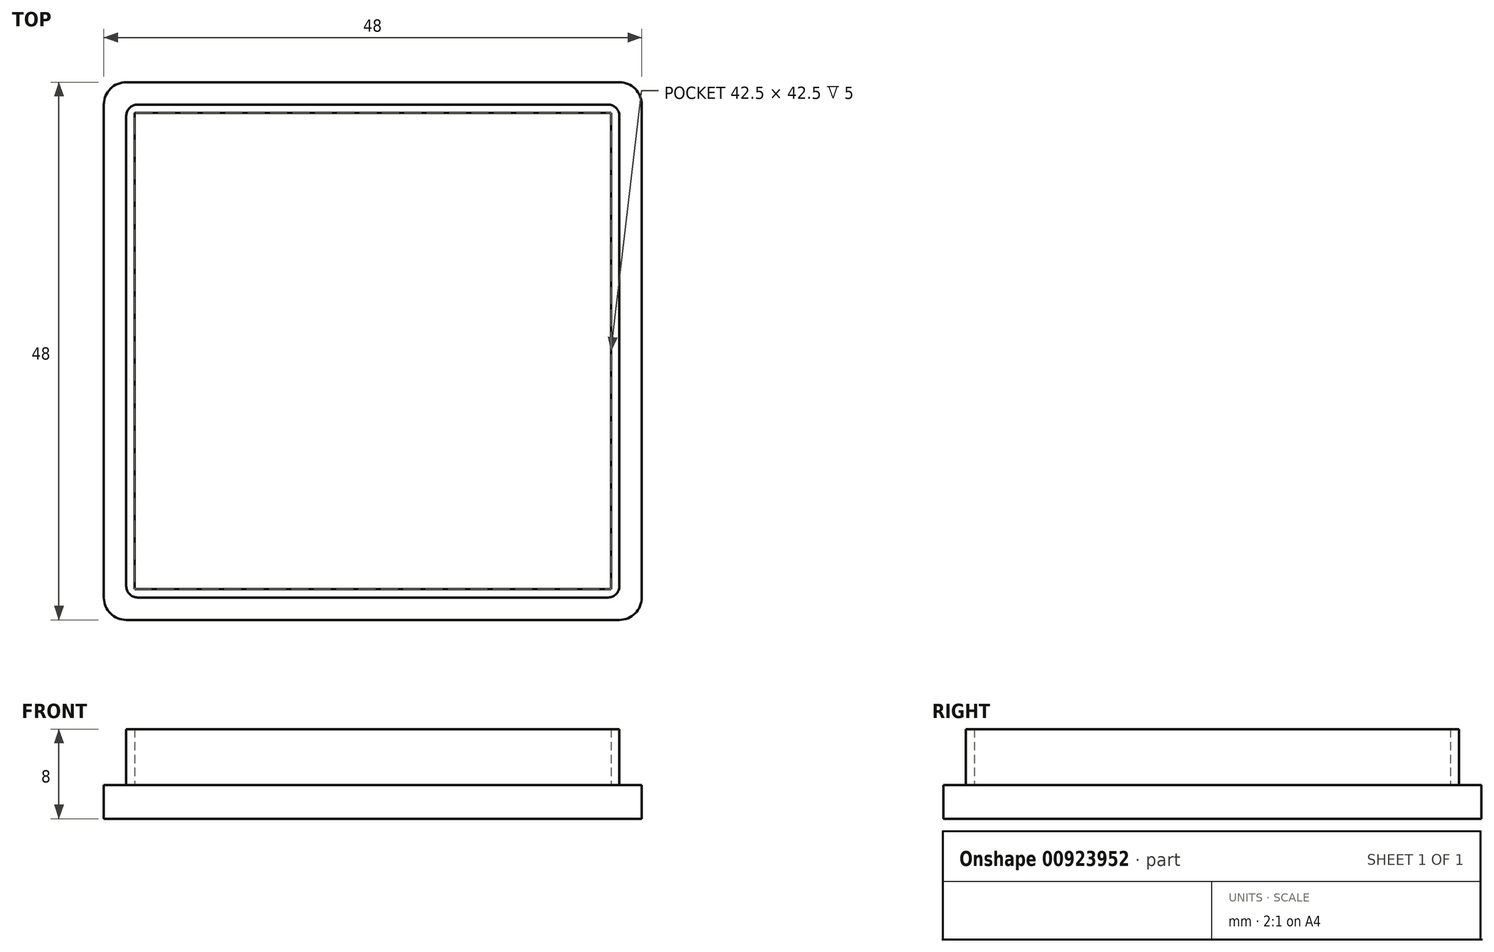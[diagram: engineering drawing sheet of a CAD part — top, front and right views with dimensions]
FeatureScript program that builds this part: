
annotation { "Feature Type Name" : "Feature", "Feature Type Description" : "" }
export const myFeature = defineFeature(function(context is Context, id is Id, definition is map)
    precondition{}
    {
        {
            var Q0;
            Q0=qCreatedBy(makeId("Top.planeOp"),FACE);
            var sketch = newSketch(context, id + "F0", { "sketchPlane" : qUnion([Q0])});
            skLineSegment(sketch, "E0.bottom", {"start": v(0, 0) * mm, "end": v(48, 0) * mm});
            skLineSegment(sketch, "E0.top", {"start": v(0, -48) * mm, "end": v(48, -48) * mm});
            skLineSegment(sketch, "E0.left", {"start": v(0, 0) * mm, "end": v(0, -48) * mm});
            skLineSegment(sketch, "E0.right", {"start": v(48, 0) * mm, "end": v(48, -48) * mm});
            skSolve(sketch);
        }
        {
            var Q0;
            Q0=makeQuery(id+"F0.imprint","IMPRINT",FACE,{"disambiguationData":[TD([[makeQuery(id+"F0.imprint","IMPRINT",EDGE,{"derivedFrom":sQuery(id+"F0.wireOp",EDGE,"E0.bottom")}),-1.0]])]});
            extrude(context, id + "F1", {"entities" : qUnion([Q0]), "depth" : 3 * mm, "offsetDistance" : 25 * mm});
        }
        {
            var Q0;
            Q0=makeQuery(id+"F1.opExtrude","SWEPT_EDGE",EDGE,{"disambiguationData":[OSD([sQuery(id+"F0.wireOp",EDGE,"E0.top"),sQuery(id+"F0.wireOp",EDGE,"E0.right")])]});
            var Q1;
            Q1=makeQuery(id+"F1.opExtrude","SWEPT_EDGE",EDGE,{"disambiguationData":[OSD([sQuery(id+"F0.wireOp",EDGE,"E0.top"),sQuery(id+"F0.wireOp",EDGE,"E0.left")])]});
            var Q2;
            Q2=makeQuery(id+"F1.opExtrude","SWEPT_EDGE",EDGE,{"disambiguationData":[OSD([sQuery(id+"F0.wireOp",EDGE,"E0.bottom"),sQuery(id+"F0.wireOp",EDGE,"E0.right")])]});
            var Q3;
            Q3=makeQuery(id+"F1.opExtrude","SWEPT_EDGE",EDGE,{"disambiguationData":[OSD([sQuery(id+"F0.wireOp",EDGE,"E0.bottom"),sQuery(id+"F0.wireOp",EDGE,"E0.left")])]});
            fillet(context, id + "F2", {"entities" : qUnion([Q0, Q1, Q2, Q3]), "radius" : 2 * mm, "tangentPropagation" : true, "allowEdgeOverflow" : false});
        }
        {
            var Q0;
            Q0=makeQuery(id+"F1.opExtrude","CAP_FACE",FACE,{"disambiguationData":[OSD([sQuery(id+"F0.wireOp",EDGE,"E0.bottom"),sQuery(id+"F0.wireOp",EDGE,"E0.top"),sQuery(id+"F0.wireOp",EDGE,"E0.left"),sQuery(id+"F0.wireOp",EDGE,"E0.right")])],"isStart":false});
            var sketch = newSketch(context, id + "F3", { "sketchPlane" : qUnion([Q0])});
            skPoint(sketch, "E1", {"position": v(24, -24) * mm});
            skPoint(sketch, "E1.positionSnap0", {"position": v(24, 0) * mm});
            skPoint(sketch, "E1.positionSnap1", {"position": v(48, -24) * mm});
            skLineSegment(sketch, "E2.bottom", {"start": v(46, -2) * mm, "end": v(2, -2) * mm});
            skLineSegment(sketch, "E2.top", {"start": v(46, -46) * mm, "end": v(2, -46) * mm});
            skLineSegment(sketch, "E2.left", {"start": v(46, -2) * mm, "end": v(46, -46) * mm});
            skLineSegment(sketch, "E2.right", {"start": v(2, -2) * mm, "end": v(2, -46) * mm});
            skLineSegment(sketch, "E3.bottom", {"start": v(45.25, -45.25) * mm, "end": v(2.75, -45.25) * mm});
            skLineSegment(sketch, "E3.top", {"start": v(45.25, -2.75) * mm, "end": v(2.75, -2.75) * mm});
            skLineSegment(sketch, "E3.left", {"start": v(45.25, -45.25) * mm, "end": v(45.25, -2.75) * mm});
            skLineSegment(sketch, "E3.right", {"start": v(2.75, -45.25) * mm, "end": v(2.75, -2.75) * mm});
            skSolve(sketch);
        }
        {
            var Q0;
            Q0=makeQuery(id+"F3.imprint","IMPRINT",FACE,{"disambiguationData":[TD([[makeQuery(id+"F3.imprint","IMPRINT",EDGE,{"derivedFrom":sQuery(id+"F3.wireOp",EDGE,"E2.bottom")}),1.0]])]});
            extrude(context, id + "F4", {"entities" : qUnion([Q0]), "operationType" : NewBodyOperationType.ADD, "depth" : 5 * mm, "offsetDistance" : 25 * mm});
        }
        {
            var Q0;
            Q0=makeQuery(id+"F4.opExtrude","SWEPT_EDGE",EDGE,{"disambiguationData":[OSD([sQuery(id+"F3.wireOp",EDGE,"E2.bottom"),sQuery(id+"F3.wireOp",EDGE,"E2.left")])]});
            var Q1;
            Q1=makeQuery(id+"F4.opExtrude","SWEPT_EDGE",EDGE,{"disambiguationData":[OSD([sQuery(id+"F3.wireOp",EDGE,"E2.bottom"),sQuery(id+"F3.wireOp",EDGE,"E2.right")])]});
            var Q2;
            Q2=makeQuery(id+"F4.opExtrude","SWEPT_EDGE",EDGE,{"disambiguationData":[OSD([sQuery(id+"F3.wireOp",EDGE,"E2.top"),sQuery(id+"F3.wireOp",EDGE,"E2.right")])]});
            var Q3;
            Q3=makeQuery(id+"F4.opExtrude","SWEPT_EDGE",EDGE,{"disambiguationData":[OSD([sQuery(id+"F3.wireOp",EDGE,"E2.top"),sQuery(id+"F3.wireOp",EDGE,"E2.left")])]});
            fillet(context, id + "F5", {"entities" : qUnion([Q0, Q1, Q2, Q3]), "radius" : 1 * mm, "tangentPropagation" : true, "allowEdgeOverflow" : false});
        }
    });
